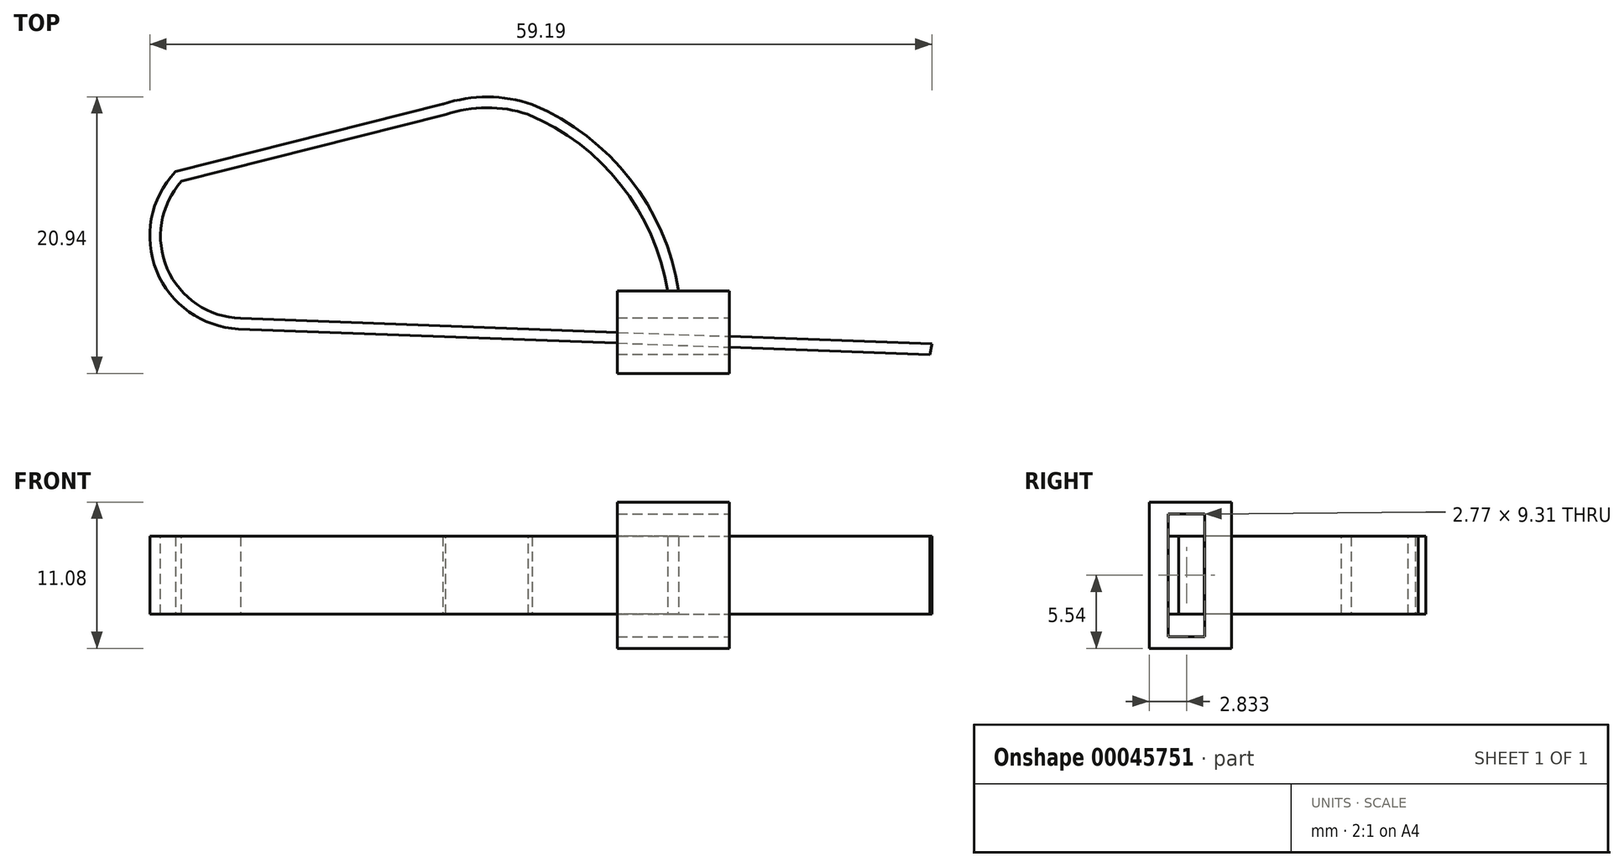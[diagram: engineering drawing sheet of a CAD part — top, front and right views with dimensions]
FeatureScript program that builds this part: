
annotation { "Feature Type Name" : "Feature", "Feature Type Description" : "" }
export const myFeature = defineFeature(function(context is Context, id is Id, definition is map)
    precondition{}
    {
        {
            var Q0;
            Q0=qCreatedBy(makeId("Right.planeOp"),FACE);
            var sketch = newSketch(context, id + "F0", { "sketchPlane" : qUnion([Q0])});
            skLineSegment(sketch, "E0.rect.bottom", {"start": v(34.4, -5.54) * mm, "end": v(28.15, -5.54) * mm});
            skLineSegment(sketch, "E0.rect.top", {"start": v(34.4, 5.54) * mm, "end": v(28.15, 5.54) * mm});
            skLineSegment(sketch, "E0.rect.left", {"start": v(34.4, -5.54) * mm, "end": v(34.4, 5.54) * mm});
            skLineSegment(sketch, "E0.rect.right", {"start": v(28.15, -5.54) * mm, "end": v(28.15, 5.54) * mm});
            skPoint(sketch, "E0.rect.middle", {"position": v(31.27, 0) * mm});
            skSolve(sketch);
        }
        {
            var Q0;
            Q0=makeQuery(id+"F0.imprint","IMPRINT",FACE,{"disambiguationData":[TD([[makeQuery(id+"F0.imprint","IMPRINT",EDGE,{"derivedFrom":sQuery(id+"F0.wireOp",EDGE,"E0.rect.bottom")}),-1.0]])]});
            extrude(context, id + "F1", {"entities" : qUnion([Q0]), "endBound" : BoundingType.SYMMETRIC, "depth" : 8.47 * mm});
        }
        {
            var Q0;
            Q0=makeQuery(id+"F1.opExtrude","CAP_FACE",FACE,{"disambiguationData":[OSD([sQuery(id+"F0.wireOp",EDGE,"E0.rect.bottom"),sQuery(id+"F0.wireOp",EDGE,"E0.rect.top"),sQuery(id+"F0.wireOp",EDGE,"E0.rect.left"),sQuery(id+"F0.wireOp",EDGE,"E0.rect.right")])],"isStart":false});
            var sketch = newSketch(context, id + "F2", { "sketchPlane" : qUnion([Q0])});
            skLineSegment(sketch, "E1.rect.bottom", {"start": v(29.6, -4.65) * mm, "end": v(32.37, -4.65) * mm});
            skLineSegment(sketch, "E1.rect.top", {"start": v(29.6, 4.65) * mm, "end": v(32.37, 4.65) * mm});
            skLineSegment(sketch, "E1.rect.left", {"start": v(29.6, -4.65) * mm, "end": v(29.6, 4.65) * mm});
            skLineSegment(sketch, "E1.rect.right", {"start": v(32.37, -4.65) * mm, "end": v(32.37, 4.65) * mm});
            skPoint(sketch, "E1.rect.middle", {"position": v(30.98, 0) * mm});
            skSolve(sketch);
        }
        {
            var Q0;
            Q0=makeQuery(id+"F2.imprint","IMPRINT",FACE,{"disambiguationData":[TD([[makeQuery(id+"F2.imprint","IMPRINT",EDGE,{"derivedFrom":sQuery(id+"F2.wireOp",EDGE,"E1.rect.bottom")}),1.0]])]});
            var Q1;
            Q1=makeQuery(id+"F1.opExtrude","CAP_FACE",FACE,{"disambiguationData":[OSD([sQuery(id+"F0.wireOp",EDGE,"E0.rect.bottom"),sQuery(id+"F0.wireOp",EDGE,"E0.rect.top"),sQuery(id+"F0.wireOp",EDGE,"E0.rect.left"),sQuery(id+"F0.wireOp",EDGE,"E0.rect.right")])],"isStart":true});
            extrude(context, id + "F3", {"entities" : qUnion([Q0]), "operationType" : NewBodyOperationType.REMOVE, "endBound" : BoundingType.UP_TO_SURFACE, "oppositeDirection" : true, "endBoundEntityFace" : qUnion([Q1]), "depth" : 25.4 * mm});
        }
        {
            var Q0;
            Q0=qCreatedBy(makeId("Top.planeOp"),FACE);
            var sketch = newSketch(context, id + "F4", { "sketchPlane" : qUnion([Q0])});
            skLineSegment(sketch, "E2.0", {"start": v(4.23, 34.4) * mm, "end": v(-4.23, 34.4) * mm});
            skArc(sketch, "E3", {"start": v(0, 34.4) * mm, "mid": v(-3.63, 42.67) * mm, "end": v(-10.82, 48.15) * mm});
            skLineSegment(sketch, "E4", {"start": v(-32.82, 31.92) * mm, "end": v(-4.23, 30.86) * mm});
            skLineSegment(sketch, "E5", {"start": v(-4.23, 30.86) * mm, "end": v(19.5, 29.99) * mm});
            skArc(sketch, "E6", {"start": v(-10.82, 48.15) * mm, "mid": v(-14.08, 48.69) * mm, "end": v(-17.33, 48.15) * mm});
            skLineSegment(sketch, "E7", {"start": v(-17.33, 48.15) * mm, "end": v(-37.44, 43.07) * mm});
            skArc(sketch, "E8", {"start": v(-37.44, 43.07) * mm, "mid": v(-38.7, 36.02) * mm, "end": v(-32.82, 31.92) * mm});
            skSolve(sketch);
        }
        {
            var Q0;
            Q0=sQuery(id+"F4.wireOp",VERTEX,"E3.start");
            var Q1;
            Q1=qCreatedBy(makeId("Front.planeOp"),FACE);
            cPlane(context, id + "F5", {"entities" : qUnion([Q0, Q1]), "cplaneType" : CPlaneType.PLANE_POINT, "offset" : 152.4 * mm, "width" : 152.4 * mm, "height" : 152.4 * mm});
        }
        {
            var Q0;
            Q0=qCreatedBy(id+"F5.planeOp",FACE);
            var sketch = newSketch(context, id + "F6", { "sketchPlane" : qUnion([Q0])});
            skLineSegment(sketch, "E9.rect.bottom", {"start": v(-0.41, 2.95) * mm, "end": v(0.41, 2.95) * mm});
            skLineSegment(sketch, "E9.rect.top", {"start": v(-0.41, -2.95) * mm, "end": v(0.41, -2.95) * mm});
            skLineSegment(sketch, "E9.rect.left", {"start": v(-0.41, 2.95) * mm, "end": v(-0.41, -2.95) * mm});
            skLineSegment(sketch, "E9.rect.right", {"start": v(0.41, 2.95) * mm, "end": v(0.41, -2.95) * mm});
            skPoint(sketch, "E9.rect.middle", {"position": v(0, 0) * mm});
            skSolve(sketch);
        }
        {
            var Q0;
            Q0=makeQuery(id+"F6.imprint","IMPRINT",FACE,{"disambiguationData":[TD([[makeQuery(id+"F6.imprint","IMPRINT",EDGE,{"derivedFrom":sQuery(id+"F6.wireOp",EDGE,"E9.rect.bottom")}),-1.0]])]});
            var Q1;
            Q1=sQuery(id+"F4.wireOp",EDGE,"E3");
            var Q2;
            Q2=sQuery(id+"F4.wireOp",EDGE,"E6");
            var Q3;
            Q3=sQuery(id+"F4.wireOp",EDGE,"E7");
            var Q4;
            Q4=sQuery(id+"F4.wireOp",EDGE,"fe1829a7-38dc-4664-9c5c-2e6ba000f032");
            var Q5;
            Q5=sQuery(id+"F4.wireOp",EDGE,"E8");
            var Q6;
            Q6=sQuery(id+"F4.wireOp",EDGE,"E4");
            var Q7;
            Q7=sQuery(id+"F4.wireOp",EDGE,"E5");
            sweep(context, id + "F7", {"operationType" : NewBodyOperationType.ADD, "profiles" : qUnion([Q0]), "path" : qUnion([Q1, Q2, Q3, Q4, Q5, Q6, Q7])});
        }
    });
